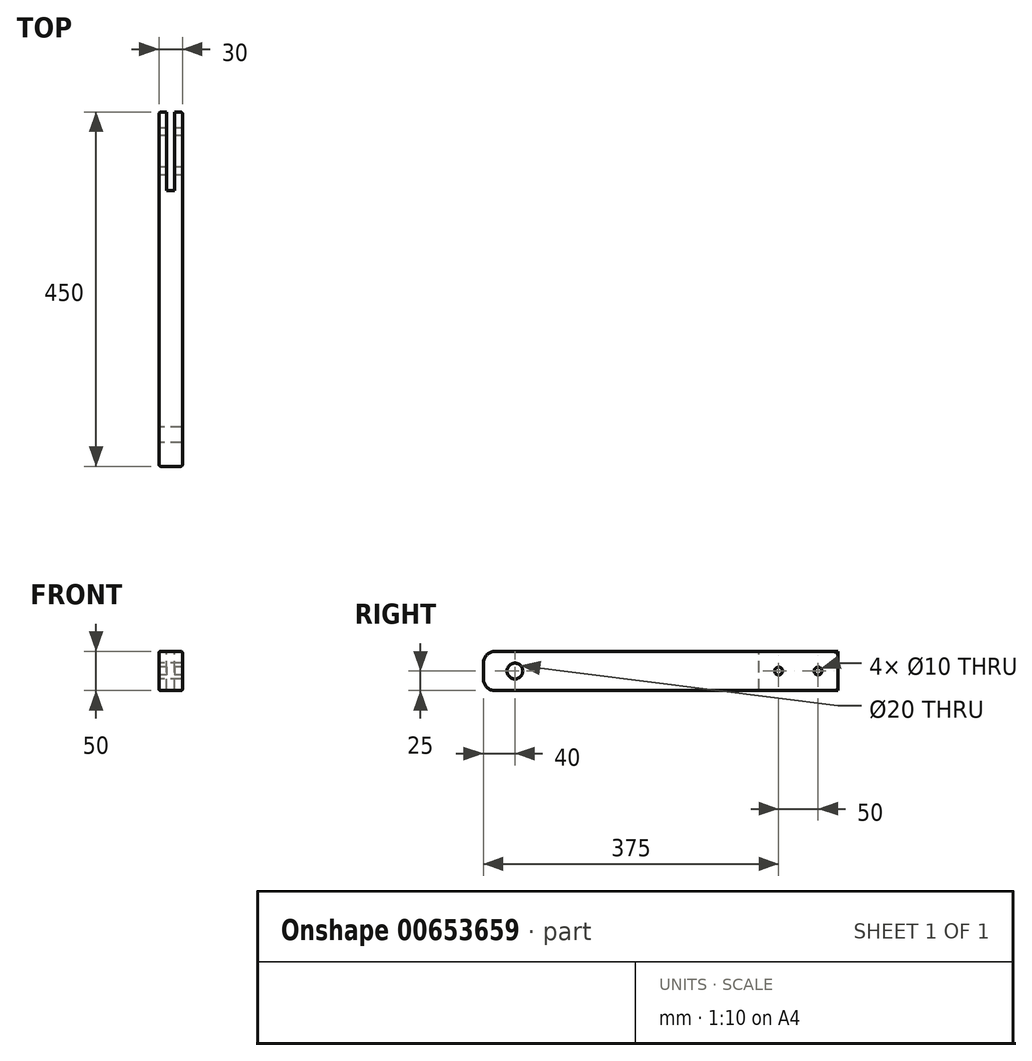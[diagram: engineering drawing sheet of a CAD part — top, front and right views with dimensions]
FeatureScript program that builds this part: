
annotation { "Feature Type Name" : "Feature", "Feature Type Description" : "" }
export const myFeature = defineFeature(function(context is Context, id is Id, definition is map)
    precondition{}
    {
        {
            var Q0;
            Q0=qCreatedBy(makeId("Right.planeOp"),FACE);
            var sketch = newSketch(context, id + "F0", { "sketchPlane" : qUnion([Q0])});
            skLineSegment(sketch, "E0.bottom", {"start": v(0, 0) * mm, "end": v(450, 0) * mm});
            skLineSegment(sketch, "E0.top", {"start": v(0, 50) * mm, "end": v(450, 50) * mm});
            skLineSegment(sketch, "E0.left", {"start": v(0, 0) * mm, "end": v(0, 50) * mm});
            skLineSegment(sketch, "E0.right", {"start": v(450, 0) * mm, "end": v(450, 50) * mm});
            skSolve(sketch);
        }
        {
            var Q0;
            Q0=makeQuery(id+"F0.imprint","IMPRINT",FACE,{"disambiguationData":[TD([[makeQuery(id+"F0.imprint","IMPRINT",EDGE,{"derivedFrom":sQuery(id+"F0.wireOp",EDGE,"E0.bottom")}),1.0]])]});
            extrude(context, id + "F1", {"entities" : qUnion([Q0]), "depth" : 30 * mm, "offsetDistance" : 25 * mm});
        }
        {
            var Q0;
            Q0=makeQuery(id+"F1.opExtrude","SWEPT_EDGE",EDGE,{"disambiguationData":[OSD([sQuery(id+"F0.wireOp",EDGE,"E0.top"),sQuery(id+"F0.wireOp",EDGE,"E0.left")])]});
            var Q1;
            Q1=makeQuery(id+"F1.opExtrude","SWEPT_EDGE",EDGE,{"disambiguationData":[OSD([sQuery(id+"F0.wireOp",EDGE,"E0.bottom"),sQuery(id+"F0.wireOp",EDGE,"E0.left")])]});
            fillet(context, id + "F2", {"entities" : qUnion([Q0, Q1]), "radius" : 15 * mm, "tangentPropagation" : true, "allowEdgeOverflow" : false});
        }
        {
            var Q0;
            Q0=makeQuery(id+"F1.opExtrude","SWEPT_FACE",FACE,{"disambiguationData":[OSD([sQuery(id+"F0.wireOp",EDGE,"E0.top")])]});
            var sketch = newSketch(context, id + "F3", { "sketchPlane" : qUnion([Q0])});
            skLineSegment(sketch, "E1.bottom", {"start": v(10, 450) * mm, "end": v(20, 450) * mm});
            skLineSegment(sketch, "E1.top", {"start": v(10, 350) * mm, "end": v(20, 350) * mm});
            skLineSegment(sketch, "E1.left", {"start": v(10, 450) * mm, "end": v(10, 350) * mm});
            skLineSegment(sketch, "E1.right", {"start": v(20, 450) * mm, "end": v(20, 350) * mm});
            skSolve(sketch);
        }
        {
            var Q0;
            Q0=makeQuery(id+"F3.imprint","IMPRINT",FACE,{"disambiguationData":[TD([[makeQuery(id+"F3.imprint","IMPRINT",EDGE,{"derivedFrom":sQuery(id+"F3.wireOp",EDGE,"E1.bottom")}),1.0]])]});
            extrude(context, id + "F4", {"entities" : qUnion([Q0]), "operationType" : NewBodyOperationType.REMOVE, "endBound" : BoundingType.THROUGH_ALL, "oppositeDirection" : true, "depth" : 25 * mm, "offsetDistance" : 25 * mm});
        }
        {
            var Q0;
            Q0=makeQuery(id+"F1.opExtrude","CAP_FACE",FACE,{"disambiguationData":[OSD([sQuery(id+"F0.wireOp",EDGE,"E0.bottom"),sQuery(id+"F0.wireOp",EDGE,"E0.top"),sQuery(id+"F0.wireOp",EDGE,"E0.left"),sQuery(id+"F0.wireOp",EDGE,"E0.right")])],"isStart":false});
            var Q1;
            Q1=makeQuery(id+"F1.opExtrude","CAP_FACE",FACE,{"disambiguationData":[OSD([sQuery(id+"F0.wireOp",EDGE,"E0.bottom"),sQuery(id+"F0.wireOp",EDGE,"E0.top"),sQuery(id+"F0.wireOp",EDGE,"E0.left"),sQuery(id+"F0.wireOp",EDGE,"E0.right")])],"isStart":true});
            fillet(context, id + "F5", {"entities" : qUnion([Q0, Q1]), "radius" : 2.5 * mm, "tangentPropagation" : true, "allowEdgeOverflow" : false});
        }
        {
            var Q0;
            Q0=makeQuery(id+"F1.opExtrude","CAP_FACE",FACE,{"disambiguationData":[OSD([sQuery(id+"F0.wireOp",EDGE,"E0.bottom"),sQuery(id+"F0.wireOp",EDGE,"E0.top"),sQuery(id+"F0.wireOp",EDGE,"E0.left"),sQuery(id+"F0.wireOp",EDGE,"E0.right")])],"isStart":false});
            var sketch = newSketch(context, id + "F6", { "sketchPlane" : qUnion([Q0])});
            skPoint(sketch, "E2", {"position": v(375, 25) * mm});
            skPoint(sketch, "E3", {"position": v(425, 25) * mm});
            skSolve(sketch);
        }
        {
            var Q0;
            Q0=sQuery(id+"F6.wireOp",VERTEX,"E2");
            var Q1;
            Q1=sQuery(id+"F6.wireOp",VERTEX,"E3");
            var Q2;
            Q2=makeQuery(id+"F1.opExtrude","SWEPT_BODY",BODY,{"disambiguationData":[OSD([sQuery(id+"F0.wireOp",EDGE,"E0.bottom"),sQuery(id+"F0.wireOp",EDGE,"E0.top"),sQuery(id+"F0.wireOp",EDGE,"E0.left"),sQuery(id+"F0.wireOp",EDGE,"E0.right")])]});
            hole(context, id + "F7", {"style" : HoleStyle.SIMPLE, "endStyle" : HoleEndStyle.BLIND, "holeDiameter" : 10 * mm, "majorDiameter" : 5 * mm, "holeDepth" : 100 * mm, "isTappedThrough" : true, "tappedDepth" : 12 * mm, "tapClearance" : 3, "locations" : qUnion([Q0, Q1]), "scope" : qUnion([Q2])});
        }
        {
            var Q0;
            Q0=makeQuery(id+"F1.opExtrude","CAP_FACE",FACE,{"disambiguationData":[OSD([sQuery(id+"F0.wireOp",EDGE,"E0.bottom"),sQuery(id+"F0.wireOp",EDGE,"E0.top"),sQuery(id+"F0.wireOp",EDGE,"E0.left"),sQuery(id+"F0.wireOp",EDGE,"E0.right")])],"isStart":true});
            var sketch = newSketch(context, id + "F8", { "sketchPlane" : qUnion([Q0])});
            skCircle(sketch, "E4", {"center": v(-40, 25) * mm, "radius": 10 * mm});
            skSolve(sketch);
        }
        {
            var Q0;
            Q0=makeQuery(id+"F8.imprint","IMPRINT",FACE,{"disambiguationData":[TD([[makeQuery(id+"F8.imprint","IMPRINT",EDGE,{"derivedFrom":sQuery(id+"F8.wireOp",EDGE,"E4")}),1.0]])]});
            extrude(context, id + "F9", {"entities" : qUnion([Q0]), "operationType" : NewBodyOperationType.REMOVE, "endBound" : BoundingType.THROUGH_ALL, "oppositeDirection" : true, "depth" : 25 * mm, "offsetDistance" : 25 * mm});
        }
    });
